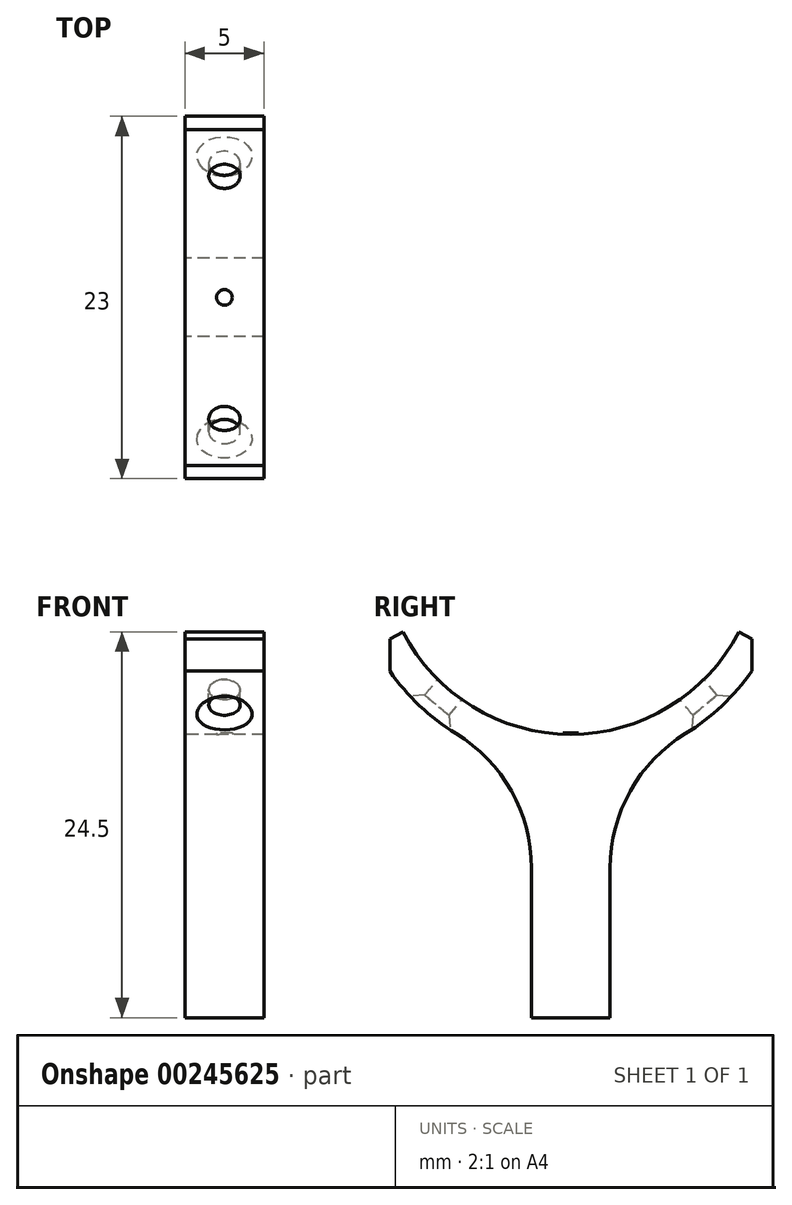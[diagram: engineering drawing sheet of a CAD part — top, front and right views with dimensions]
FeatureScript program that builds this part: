
annotation { "Feature Type Name" : "Feature", "Feature Type Description" : "" }
export const myFeature = defineFeature(function(context is Context, id is Id, definition is map)
    precondition{}
    {
        {
            var Q0;
            Q0=qCreatedBy(makeId("Right.planeOp"),FACE);
            var sketch = newSketch(context, id + "F0", { "sketchPlane" : qUnion([Q0])});
            skArc(sketch, "E0", {"start": v(7.3, -11.95) * mm, "mid": v(9.6, -10.19) * mm, "end": v(11.5, -7.98) * mm});
            skArc(sketch, "E1", {"start": v(-10.67, -5.5) * mm, "mid": v(0, -12) * mm, "end": v(10.67, -5.5) * mm});
            skLineSegment(sketch, "E2", {"start": v(-2.5, -30) * mm, "end": v(2.5, -30) * mm});
            skLineSegment(sketch, "E3", {"start": v(2.5, -30) * mm, "end": v(2.5, -20.49) * mm});
            skLineSegment(sketch, "E4", {"start": v(-2.5, -30) * mm, "end": v(-2.5, -20.49) * mm});
            skPoint(sketch, "E5.visualSharp", {"position": v(2.5, -13.77) * mm});
            skArc(sketch, "E5.filletArc", {"start": v(7.3, -11.95) * mm, "mid": v(3.78, -15.6) * mm, "end": v(2.5, -20.49) * mm});
            skPoint(sketch, "E6.visualSharp", {"position": v(-2.5, -13.77) * mm});
            skArc(sketch, "E6.filletArc", {"start": v(-2.5, -20.49) * mm, "mid": v(-3.78, -15.6) * mm, "end": v(-7.3, -11.95) * mm});
            skPoint(sketch, "E7.endSnap0", {"position": v(0, -30) * mm});
            skArc(sketch, "E8.trimOffspring", {"start": v(-11.5, -7.98) * mm, "mid": v(-9.6, -10.19) * mm, "end": v(-7.3, -11.95) * mm});
            skPoint(sketch, "E9.orphan", {"position": v(0, -5.5) * mm});
            skLineSegment(sketch, "E10", {"start": v(-11.5, -5.93) * mm, "end": v(-11.5, -7.98) * mm});
            skLineSegment(sketch, "E11", {"start": v(11.5, -5.93) * mm, "end": v(11.5, -7.98) * mm});
            skLineSegment(sketch, "E12", {"start": v(-10.67, -5.5) * mm, "end": v(-11.5, -5.93) * mm});
            skLineSegment(sketch, "E13", {"start": v(10.67, -5.5) * mm, "end": v(11.5, -5.93) * mm});
            skPoint(sketch, "E14.orphan", {"position": v(11.5, -5.5) * mm});
            skPoint(sketch, "E15.end.orphan", {"position": v(-11.5, -5.5) * mm});
            skPoint(sketch, "E7.start.orphan", {"position": v(0, -30) * mm});
            skSolve(sketch);
        }
        {
            var Q0;
            Q0=makeQuery(id+"F0.imprint","IMPRINT",FACE,{"disambiguationData":[TD([[makeQuery(id+"F0.imprint","IMPRINT",EDGE,{"derivedFrom":sQuery(id+"F0.wireOp",EDGE,"E0")}),1.0]])]});
            extrude(context, id + "F1", {"entities" : qUnion([Q0]), "depth" : 5 * mm});
        }
        {
            var Q0;
            Q0=makeQuery(id+"F1.opExtrude","CAP_FACE",FACE,{"disambiguationData":[OSD([sQuery(id+"F0.wireOp",EDGE,"E0"),sQuery(id+"F0.wireOp",EDGE,"E1"),sQuery(id+"F0.wireOp",EDGE,"E2"),sQuery(id+"F0.wireOp",EDGE,"E3"),sQuery(id+"F0.wireOp",EDGE,"E4"),sQuery(id+"F0.wireOp",EDGE,"E5.filletArc"),sQuery(id+"F0.wireOp",EDGE,"E6.filletArc"),sQuery(id+"F0.wireOp",EDGE,"E8.trimOffspring"),sQuery(id+"F0.wireOp",EDGE,"E10"),sQuery(id+"F0.wireOp",EDGE,"E11"),sQuery(id+"F0.wireOp",EDGE,"E12"),sQuery(id+"F0.wireOp",EDGE,"E13")])],"isStart":false});
            var sketch = newSketch(context, id + "F2", { "sketchPlane" : qUnion([Q0])});
            skLineSegment(sketch, "E16", {"start": v(0, 0) * mm, "end": v(-9, -10.72) * mm});
            skLineSegment(sketch, "E17", {"start": v(0, 0) * mm, "end": v(9, -10.72) * mm});
            skSolve(sketch);
        }
        {
            var Q0;
            Q0=sQuery(id+"F2.wireOp",EDGE,"E16");
            var Q1;
            Q1=sQuery(id+"F2.wireOp",VERTEX,"E16.end");
            cPlane(context, id + "F3", {"entities" : qUnion([Q0, Q1]), "cplaneType" : CPlaneType.CURVE_POINT, "offset" : 25 * mm, "width" : 150 * mm, "height" : 150 * mm});
        }
        {
            var Q0;
            Q0=qCreatedBy(id+"F3.planeOp",FACE);
            var sketch = newSketch(context, id + "F4", { "sketchPlane" : qUnion([Q0])});
            skPoint(sketch, "E18", {"position": v(2.5, 0) * mm});
            skSolve(sketch);
        }
        {
            var Q0;
            Q0=sQuery(id+"F4.wireOp",VERTEX,"E18");
            var Q1;
            Q1=makeQuery(id+"F1.opExtrude","SWEPT_BODY",BODY,{"disambiguationData":[OSD([sQuery(id+"F0.wireOp",EDGE,"E0"),sQuery(id+"F0.wireOp",EDGE,"E1"),sQuery(id+"F0.wireOp",EDGE,"E2"),sQuery(id+"F0.wireOp",EDGE,"E3"),sQuery(id+"F0.wireOp",EDGE,"E4"),sQuery(id+"F0.wireOp",EDGE,"E5.filletArc"),sQuery(id+"F0.wireOp",EDGE,"E6.filletArc"),sQuery(id+"F0.wireOp",EDGE,"E8.trimOffspring"),sQuery(id+"F0.wireOp",EDGE,"E10"),sQuery(id+"F0.wireOp",EDGE,"E11"),sQuery(id+"F0.wireOp",EDGE,"E12"),sQuery(id+"F0.wireOp",EDGE,"E13")])]});
            hole(context, id + "F5", {"style" : HoleStyle.C_SINK, "endStyle" : HoleEndStyle.BLIND, "holeDiameter" : 2 * mm, "cSinkDiameter" : 3.5 * mm, "cSinkAngle" : 90 * degree, "holeDepth" : 5 * mm, "tappedDepth" : 15 * mm, "tapClearance" : 0, "locations" : qUnion([Q0]), "scope" : qUnion([Q1]), "startStyle" : HoleStartStyle.SKETCH});
        }
        {
            var Q0;
            Q0=sQuery(id+"F2.wireOp",EDGE,"E17");
            var Q1;
            Q1=sQuery(id+"F2.wireOp",VERTEX,"E17.end");
            cPlane(context, id + "F6", {"entities" : qUnion([Q0, Q1]), "cplaneType" : CPlaneType.CURVE_POINT, "offset" : 25 * mm, "width" : 150 * mm, "height" : 150 * mm});
        }
        {
            var Q0;
            Q0=qCreatedBy(id+"F6.planeOp",FACE);
            var sketch = newSketch(context, id + "F7", { "sketchPlane" : qUnion([Q0])});
            skPoint(sketch, "E19", {"position": v(2.5, 0) * mm});
            skSolve(sketch);
        }
        {
            var Q0;
            Q0=sQuery(id+"F7.wireOp",VERTEX,"E19");
            var Q1;
            Q1=makeQuery(id+"F1.opExtrude","SWEPT_BODY",BODY,{"disambiguationData":[OSD([sQuery(id+"F0.wireOp",EDGE,"E0"),sQuery(id+"F0.wireOp",EDGE,"E1"),sQuery(id+"F0.wireOp",EDGE,"E2"),sQuery(id+"F0.wireOp",EDGE,"E3"),sQuery(id+"F0.wireOp",EDGE,"E4"),sQuery(id+"F0.wireOp",EDGE,"E5.filletArc"),sQuery(id+"F0.wireOp",EDGE,"E6.filletArc"),sQuery(id+"F0.wireOp",EDGE,"E8.trimOffspring"),sQuery(id+"F0.wireOp",EDGE,"E10"),sQuery(id+"F0.wireOp",EDGE,"E11"),sQuery(id+"F0.wireOp",EDGE,"E12"),sQuery(id+"F0.wireOp",EDGE,"E13")])]});
            hole(context, id + "F8", {"style" : HoleStyle.C_SINK, "endStyle" : HoleEndStyle.BLIND, "holeDiameter" : 2 * mm, "cSinkDiameter" : 3.5 * mm, "cSinkAngle" : 90 * degree, "holeDepth" : 5 * mm, "tappedDepth" : 15 * mm, "tapClearance" : 0, "locations" : qUnion([Q0]), "scope" : qUnion([Q1]), "startStyle" : HoleStartStyle.SKETCH});
        }
        {
            var Q0;
            Q0=qCreatedBy(makeId("Top.planeOp"),FACE);
            cPlane(context, id + "F9", {"entities" : qUnion([Q0]), "cplaneType" : CPlaneType.OFFSET, "offset" : 12 * mm, "oppositeDirection" : true, "width" : 150 * mm, "height" : 150 * mm});
        }
        {
            var Q0;
            Q0=qCreatedBy(id+"F9.planeOp",FACE);
            var sketch = newSketch(context, id + "F10", { "sketchPlane" : qUnion([Q0])});
            skPoint(sketch, "E20", {"position": v(2.5, 0) * mm});
            skCircle(sketch, "E21", {"center": v(2.5, 0) * mm, "radius": 0.5 * mm});
            skSolve(sketch);
        }
        {
            var Q0;
            Q0=makeQuery(id+"F10.imprint","IMPRINT",FACE,{"disambiguationData":[TD([[makeQuery(id+"F10.imprint","IMPRINT",EDGE,{"derivedFrom":sQuery(id+"F10.wireOp",EDGE,"E21")}),1.0]])]});
            extrude(context, id + "F11", {"entities" : qUnion([Q0]), "operationType" : NewBodyOperationType.ADD, "depth" : .1 * mm});
        }
    });
